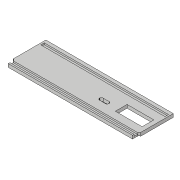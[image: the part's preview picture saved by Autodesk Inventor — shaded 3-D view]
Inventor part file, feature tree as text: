
AUTODESK INVENTOR PART (.ipt)
format: ipt  version: 2018.3 (Build 223284000, 284)  size: 158,208 bytes
history: native  units: in
note: dims shown in document units (in); Inventor stores cm internally (conversion verified against a paired STEP export)
features: extrude x6, sketch x6, fillet x3
ambient origin geometry x8: Origin, YZ Plane, XZ Plane, XY Plane, X Axis, Y Axis, Z Axis, Center Point
bodies: Solid1 (feature_tree)
feature tree (15):
  extrude  "Extrusion1"  Depth=1.5in
  extrude  "Extrusion2"  Depth=0.126in
  extrude  "Extrusion3"  Depth=0.0625in TaperAngle=0.0deg
  extrude  "Extrusion4"  Depth=0.135in
  fillet  "Fillet1"  Radius=0.0625in
  fillet  "Fillet2"  Radius=0.0625in
  extrude  "Extrusion5"  Depth=0.0625in
  fillet  "Fillet3"  Radius=0.125in
  extrude  "Extrusion6"  Depth=0.0625in TaperAngle=0.0deg
  sketch  "Sketch1"  dims[d0=4.875in d1=1.5in]
  sketch  "Sketch2"  dims[d2=0.125in d3=0.0in d6=0.126in]
  sketch  "Sketch3"  dims[d7=0.0625in d8=0.0625in d9=0.0in]
  sketch  "Sketch4"  dims[d10=0.125in d11=0.135in d12=0.0625in d13=0.0625in]
  sketch  "Sketch5"  dims[d14=0.0625in d15=0.0625in d16=0.125in]
  sketch  "Sketch6"  dims[d17=0.135in d18=0.0625in d19=0.0in d20=0.0625in d21=0.25in d22=0.25in d23=0.0625in d24=1.0in d25=0.0in d26=0.0625in d27=0.0625in d28=0.3425in d29=0.14in d30=0.36in d32=1.0in d33=0.0in d34=0.0625in d35=1.025in d36=0.45in d38=1.0in d39=0.0in d41=0.28in d43=0.1in d44=1.5in]
